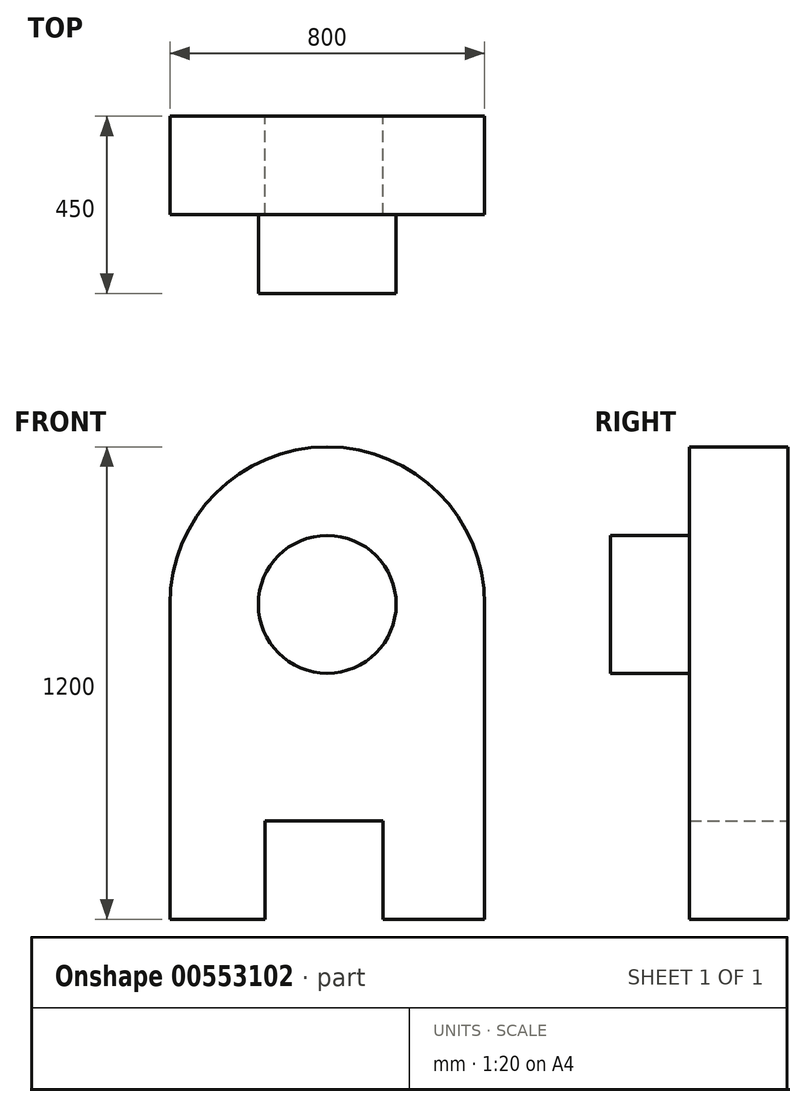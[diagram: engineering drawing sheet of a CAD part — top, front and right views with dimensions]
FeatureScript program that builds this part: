
annotation { "Feature Type Name" : "Feature", "Feature Type Description" : "" }
export const myFeature = defineFeature(function(context is Context, id is Id, definition is map)
    precondition{}
    {
        {
            var Q0;
            Q0=qCreatedBy(makeId("Front.planeOp"),FACE);
            var sketch = newSketch(context, id + "F0", { "sketchPlane" : qUnion([Q0])});
            skArc(sketch, "E0", {"start": v(400, 0) * mm, "mid": v(0, 400) * mm, "end": v(-400, 0) * mm});
            skLineSegment(sketch, "E1", {"start": v(-400, 0) * mm, "end": v(400, 0) * mm});
            skLineSegment(sketch, "E2", {"start": v(-400, 0) * mm, "end": v(-400, -800) * mm});
            skLineSegment(sketch, "E3", {"start": v(-400, -800) * mm, "end": v(-157.93, -800) * mm});
            skLineSegment(sketch, "E4", {"start": v(400, -800) * mm, "end": v(400, 0) * mm});
            skLineSegment(sketch, "E5", {"start": v(400, -800) * mm, "end": v(142.07, -800) * mm});
            skLineSegment(sketch, "E6", {"start": v(-157.93, -800) * mm, "end": v(-157.93, -550) * mm});
            skLineSegment(sketch, "E7", {"start": v(-157.93, -550) * mm, "end": v(142.07, -550) * mm});
            skLineSegment(sketch, "E8", {"start": v(142.07, -550) * mm, "end": v(142.07, -800) * mm});
            skLineSegment(sketch, "E9.trimOffspring", {"start": v(142.07, -800) * mm, "end": v(400, -800) * mm});
            skSolve(sketch);
        }
        {
            var Q0;
            Q0 = qSketchRegion(id + "F0", true);
            extrude(context, id + "F1", {"entities" : qUnion([Q0]), "depth" : 250 * mm, "offsetDistance" : 25.4 * mm});
        }
        {
            var Q0;
            Q0=makeQuery(id+"F1.opExtrude","CAP_FACE",FACE,{"disambiguationData":[OSD([sQuery(id+"F0.wireOp",EDGE,"E0"),sQuery(id+"F0.wireOp",EDGE,"E2"),sQuery(id+"F0.wireOp",EDGE,"E4"),sQuery(id+"F0.wireOp",EDGE,"E3"),sQuery(id+"F0.wireOp",EDGE,"E6"),sQuery(id+"F0.wireOp",EDGE,"E7"),sQuery(id+"F0.wireOp",EDGE,"E8"),sQuery(id+"F0.wireOp",EDGE,"E9.trimOffspring")])],"isStart":false});
            var sketch = newSketch(context, id + "F2", { "sketchPlane" : qUnion([Q0])});
            skCircle(sketch, "E10", {"center": v(0, 0) * mm, "radius": 175 * mm});
            skSolve(sketch);
        }
        {
            var Q0;
            Q0 = qSketchRegion(id + "F2", true);
            extrude(context, id + "F3", {"entities" : qUnion([Q0]), "operationType" : NewBodyOperationType.ADD, "depth" : 200 * mm, "offsetDistance" : 25.4 * mm});
        }
    });
